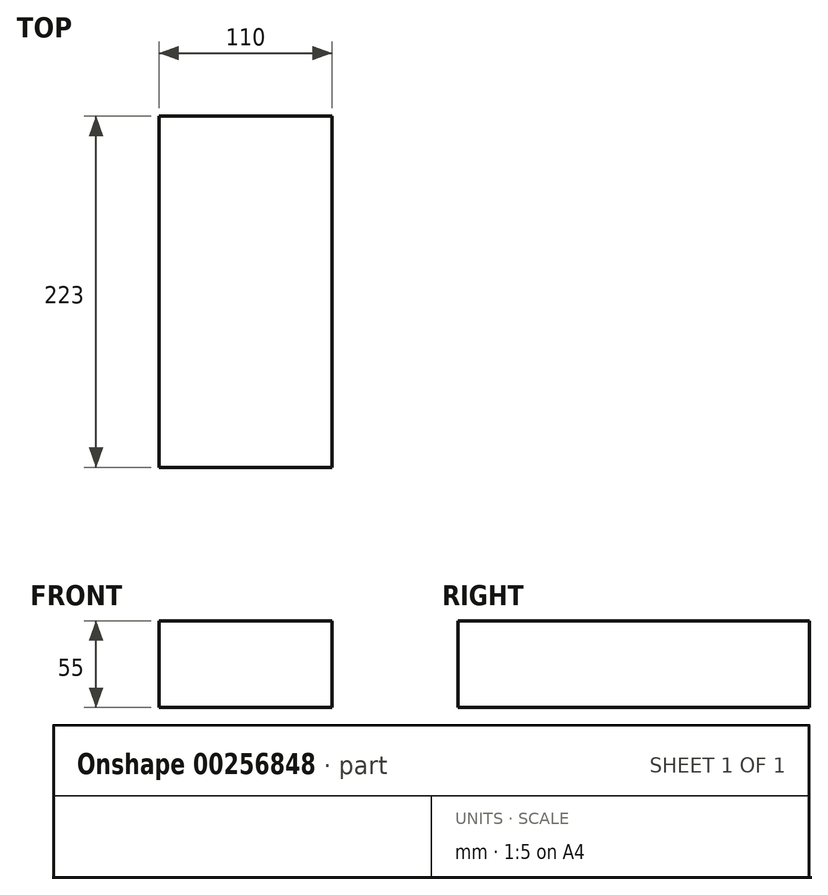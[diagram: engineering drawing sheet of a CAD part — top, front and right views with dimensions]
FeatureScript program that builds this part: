
annotation { "Feature Type Name" : "Feature", "Feature Type Description" : "" }
export const myFeature = defineFeature(function(context is Context, id is Id, definition is map)
    precondition{}
    {
        {
            var Q0;
            Q0=qCreatedBy(makeId("Front.planeOp"),FACE);
            var sketch = newSketch(context, id + "F0", { "sketchPlane" : qUnion([Q0])});
            skLineSegment(sketch, "E0.bottom", {"start": v(0, 0) * mm, "end": v(110, 0) * mm});
            skLineSegment(sketch, "E0.top", {"start": v(0, 55) * mm, "end": v(110, 55) * mm});
            skLineSegment(sketch, "E0.left", {"start": v(0, 0) * mm, "end": v(0, 55) * mm});
            skLineSegment(sketch, "E0.right", {"start": v(110, 0) * mm, "end": v(110, 55) * mm});
            skSolve(sketch);
        }
        {
            var Q0;
            Q0 = qSketchRegion(id + "F0", true);
            extrude(context, id + "F1", {"entities" : qUnion([Q0]), "depth" : 223 * mm});
        }
    });
